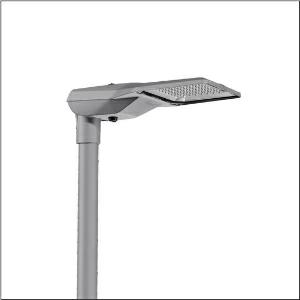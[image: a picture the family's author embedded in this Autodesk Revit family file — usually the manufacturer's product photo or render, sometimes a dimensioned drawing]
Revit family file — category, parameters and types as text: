
# Revit family: streetlight_sl_21_iq_midi___stw1_0a_5xe3e31y08nb_e460
name_source: partatom
category: Lighting Fixtures
units: mm (PartAtom-declared; Revit-internal decimal feet)

## family parameters
Cut with Voids When Loaded = No
Host = Face
Light Source = No
Part Type = Normal
Room Calculation Point = No
Round Connector Dimension = Use Diameter
Shared = No

## types (1)
- --- (1 x LED, 21550 lm, 136.6 W, 3000K)
    Apparent Load = 137 VA
    CIE Flux Codes = 39 75 98 100 100
    Color Rendering = 70
    Color Temperature = 3000K
    Default Elevation = 1800 mm
    Description = Streetlight SL 21 iQ midi, mast luminaire, primary light control with lens, of PMMA, primary optical cover: cover, of toughened safety glass, transparent, light distribution: STW1.0a, light emission: direct distribution, primary light characteristic: asymmetric, installation type: post-top, side-entry, LED, High Power LED, rated luminous flux: 21.550lm, luminous efficacy: 158lm/W, light colour: 730, colour temperature: 3000K, control: presetting dimming logarithmic, Street-Remote, Auto-Match, Temp-Guard, Lumen-Switch, Night-Set, Smart-Wire, Light-Fading, Desk-Remote (wireless, voltage-free reading and setting of iQ features in the workshop via application-optimized NFC function/RFID function), optimised constant luminous flux control (CLO 2.0), mains connection: 230..240V, AC, 50/60Hz, start of lifetime: 137W, end of service life: 144W, reduction: 61W, luminaire housing, of diecast aluminium, powder-coated, Siteco® metallic grey (DB 702S), corrosivity category C5 mid according to DIN EN ISO 12944, please order mast flange separately, inclination adjustable: 0°, 5°, 10°, 15°, sealing non-destructively replaceable, multi-level sealing system, length: 644mm, width: 335mm, height: 110mm, mast flange for spigot size: 42mm (side-entry): 5XC10008XM4, 60/48mm (side-entry/post-top): 5XC10108XM2, 76/60mm (side-entry/post-top): 5XC10108XM1, Smart Interface below and above, protection rating (complete): IP66, insulation class (complete): insulation class II (safety insulation), certification: CE, ENEC, ENEC+, VDE, impact resistance: IK09, permissible operating ambient temperature for outdoor applications: -40..+50°C, standard-compliant lighting for roads and squares, packaging unit: 1 piece

Light Distribution: STW1.0a
    Height = 111 mm
    Lamp = 1 x LED
    Lamp Light Flux = 21550 lm
    Lamp Power = 136.6 W
    Lamp count = 1
    Length = 644 mm
    Luminous efficacy = 158 lm/W
    Manufacturer = Siteco
    ModVariant = No
    Model = 5XE3E31Y08NB
    Number of Poles = 1
    OnlyDefault = Yes
    Power Factor = 1
    Product Name = Streetlight SL 21 iQ midi | STW1.0a
    Product group = mast luminaire | pylon top
    ProductGroupID = 6100
    Protection Class = Protection class II
    Protection Degree = IP 66
    RLX_Detail_Level = 1
    RLX_Emergency_Light_Flux = 0 lm
    RLX_Emergency_Type = 0
    RLX_Emergency_Type_DB = No
    RlxData = <blob elided: 91157 chars, md5=5ca85f47>
    Socket = socket
    Standby Power = 0 W
    System Light Flux = 21550 lm
    System Power = 137 W
    Type Comments = factory setting: luminous flux: 100 % | dim-lin: 254 | 733 mA
    Type Image = l_1004304.jpg
    URL = http://relux.com
    VarID = @adj_061851
    Voltage = 0 V
    Weight = 0.00 kg
    Width = 336 mm

## geometry (parser evidence)
native form markers: Blend x4, Sweep x10
no freeform markers — native parametric forms only
